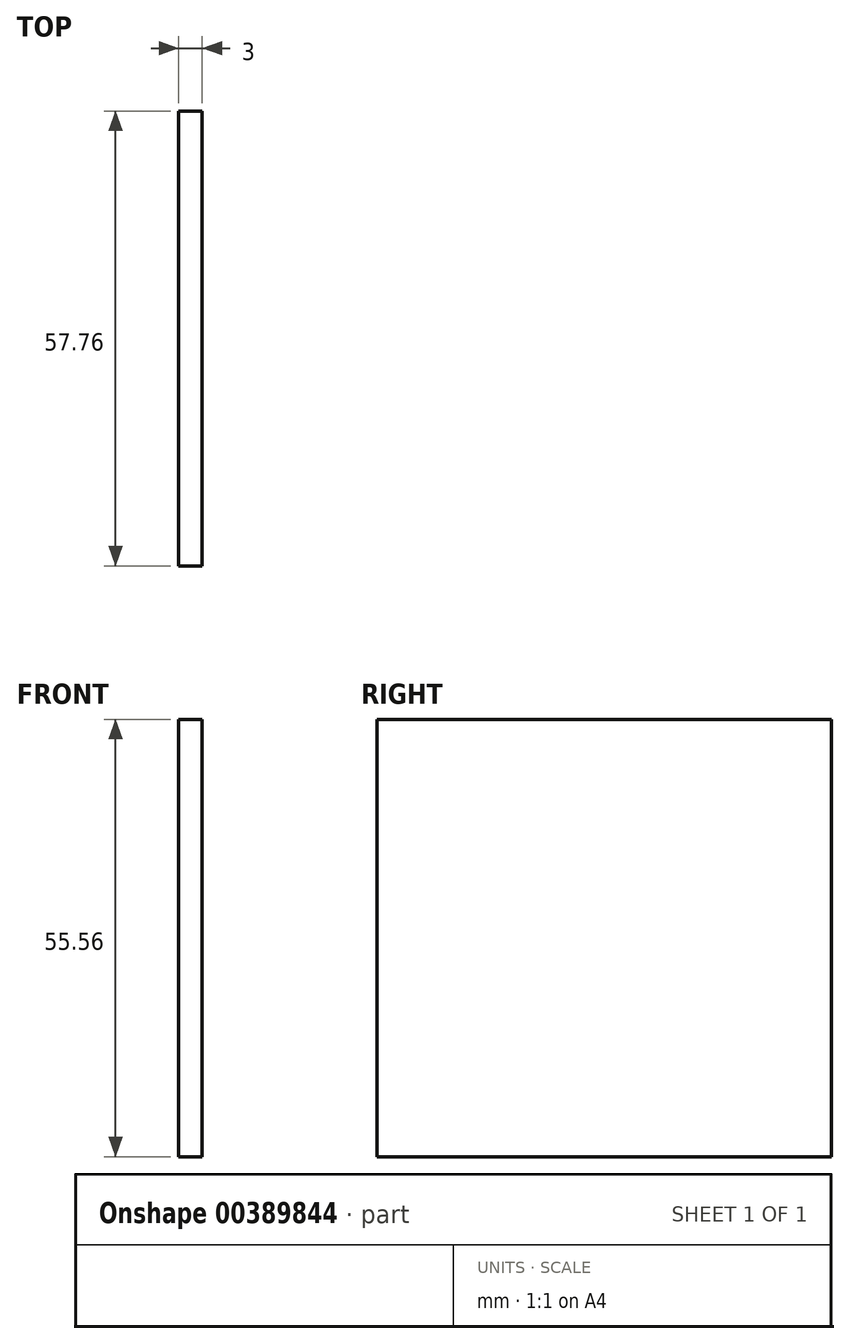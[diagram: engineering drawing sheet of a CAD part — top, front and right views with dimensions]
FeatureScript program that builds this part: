
annotation { "Feature Type Name" : "Feature", "Feature Type Description" : "" }
export const myFeature = defineFeature(function(context is Context, id is Id, definition is map)
    precondition{}
    {
        {
            var Q0;
            Q0=qCreatedBy(makeId("Right.planeOp"),FACE);
            var sketch = newSketch(context, id + "F0", { "sketchPlane" : qUnion([Q0])});
            skLineSegment(sketch, "E0.bottom", {"start": v(27.53, 26.63) * mm, "end": v(-30.23, 26.63) * mm});
            skLineSegment(sketch, "E0.top", {"start": v(27.53, -28.93) * mm, "end": v(-30.23, -28.93) * mm});
            skLineSegment(sketch, "E0.left", {"start": v(27.53, 26.63) * mm, "end": v(27.53, -28.93) * mm});
            skLineSegment(sketch, "E0.right", {"start": v(-30.23, 26.63) * mm, "end": v(-30.23, -28.93) * mm});
            skSolve(sketch);
        }
        {
            var Q0;
            Q0=makeQuery(id+"F0.imprint","IMPRINT",FACE,{"disambiguationData":[TD([[makeQuery(id+"F0.imprint","IMPRINT",EDGE,{"derivedFrom":sQuery(id+"F0.wireOp",EDGE,"E0.bottom")}),1.0]])]});
            extrude(context, id + "F1", {"entities" : qUnion([Q0]), "oppositeDirection" : true, "depth" : 3 * mm, "offsetDistance" : 25 * mm});
        }
    });
